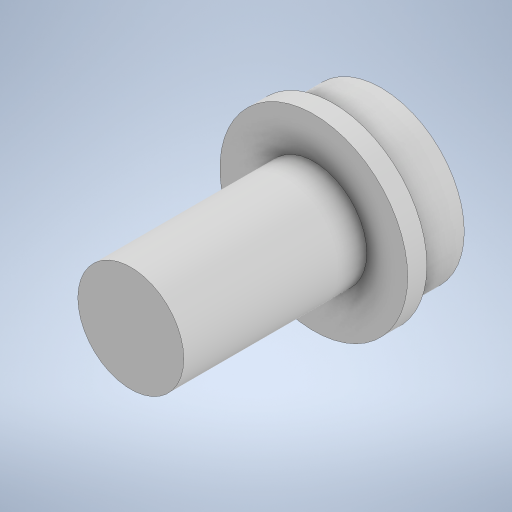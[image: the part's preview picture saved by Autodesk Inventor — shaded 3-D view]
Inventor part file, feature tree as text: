
AUTODESK INVENTOR PART (.ipt)
format: ipt  version: 2024.2 (Build 282272000, 272)  size: 231,424 bytes
history: native  units: mm
features: extrude x3, other x1, sketch x1
ambient origin geometry x8: Origin, YZ Plane, XZ Plane, XY Plane, X Axis, Y Axis, Z Axis, Center Point
bodies: Body1 (feature_tree)
feature tree (5):
  other  "Твердое тело1"
  sketch  "Эскиз1"
  extrude  "Выдавливание1"  Depth=17.25mm
  extrude  "Выдавливание2"  Depth=19.5mm
  extrude  "Выдавливание3"  Depth=11.0mm
